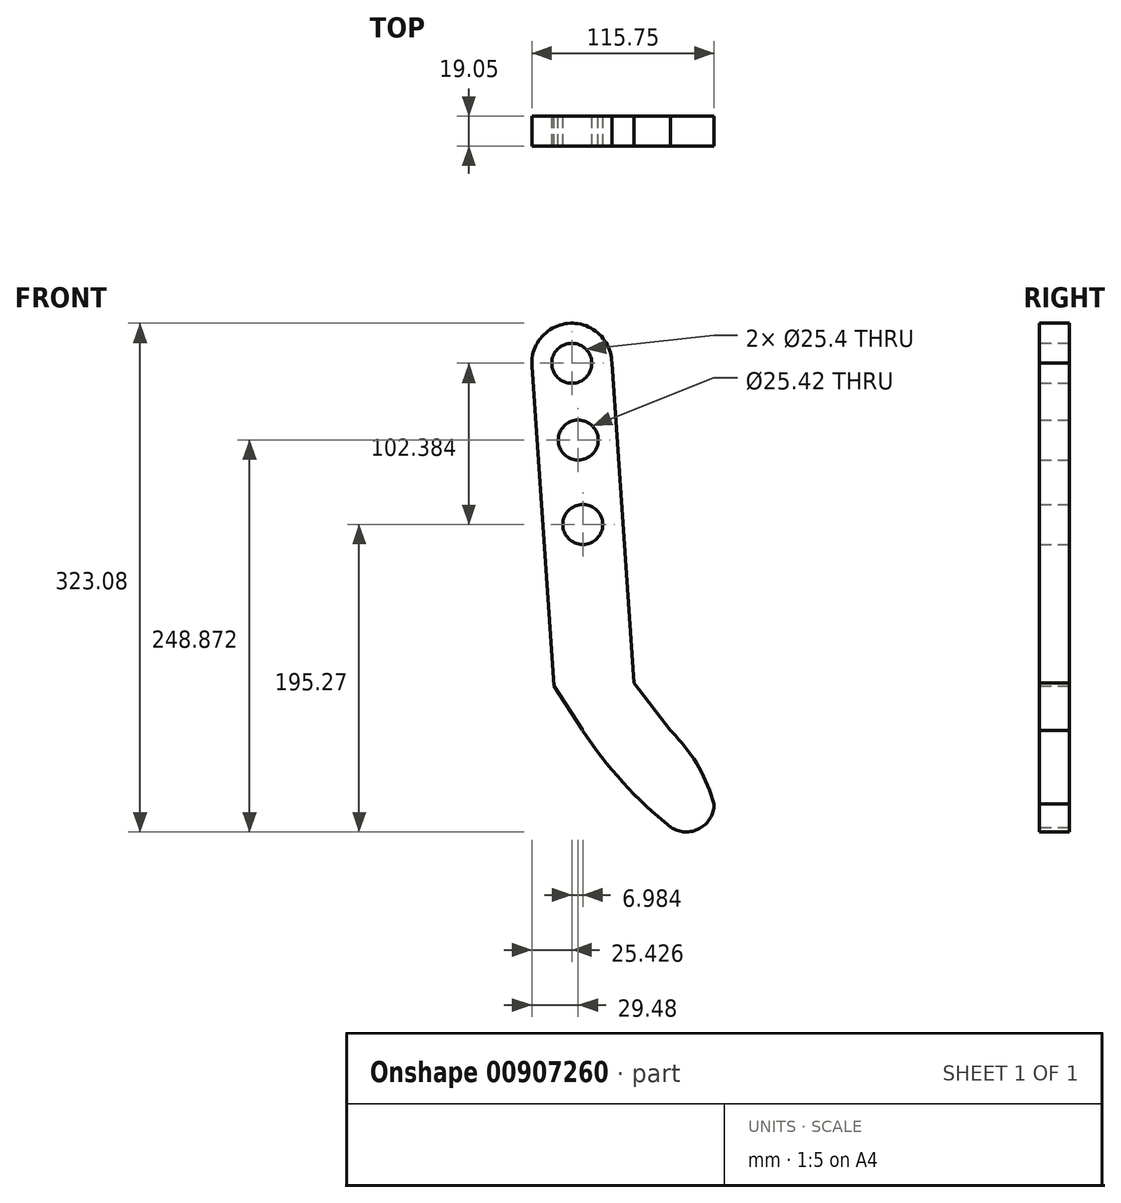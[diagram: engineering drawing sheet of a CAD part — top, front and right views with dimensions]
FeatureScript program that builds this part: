
annotation { "Feature Type Name" : "Feature", "Feature Type Description" : "" }
export const myFeature = defineFeature(function(context is Context, id is Id, definition is map)
    precondition{}
    {
        {
            var Q0;
            Q0=qCreatedBy(makeId("Front.planeOp"),FACE);
            var sketch = newSketch(context, id + "F0", { "sketchPlane" : qUnion([Q0])});
            skLineSegment(sketch, "E0.left", {"start": v(31.28, -85.06) * mm, "end": v(18.44, 102.55) * mm});
            skLineSegment(sketch, "E0.right", {"start": v(-18.44, -102.55) * mm, "end": v(-32.35, 100.65) * mm});
            skPoint(sketch, "E0.middle", {"position": v(0, 0) * mm});
            skArc(sketch, "E1", {"start": v(-32.35, 100.65) * mm, "mid": v(-7.94, 127.79) * mm, "end": v(18.44, 102.55) * mm});
            skPoint(sketch, "E2.middle", {"position": v(32.35, -100.65) * mm});
            skPoint(sketch, "E3.orphan", {"position": v(-9.8, -75.29) * mm});
            skPoint(sketch, "E2.bottom.end.orphan", {"position": v(-9.5, -126.48) * mm});
            skPoint(sketch, "E4.end.orphan", {"position": v(74.49, -126) * mm});
            skLineSegment(sketch, "E5", {"start": v(31.28, -85.06) * mm, "end": v(32.35, -100.65) * mm});
            skPoint(sketch, "E2.top.start.orphan", {"position": v(74.2, -74.82) * mm});
            skLineSegment(sketch, "E6", {"start": v(-18.44, -102.55) * mm, "end": v(27.41, -173.16) * mm});
            skLineSegment(sketch, "E7", {"start": v(27.41, -173.16) * mm, "end": v(83.34, -210.69) * mm});
            skLineSegment(sketch, "E8", {"start": v(83.34, -210.69) * mm, "end": v(83.34, -159.89) * mm});
            skLineSegment(sketch, "E9", {"start": v(83.34, -159.89) * mm, "end": v(55.72, -130.97) * mm});
            skLineSegment(sketch, "E10", {"start": v(55.72, -130.97) * mm, "end": v(32.35, -100.65) * mm});
            skCircle(sketch, "E11", {"center": v(-6.98, 102.38) * mm, "radius": 12.7 * mm});
            skSolve(sketch);
        }
        {
            var Q0;
            Q0 = qSketchRegion(id + "F0", true);
            extrude(context, id + "F1", {"entities" : qUnion([Q0]), "depth" : 19.05 * mm, "offsetDistance" : 25.4 * mm});
        }
        {
            var Q0;
            Q0=makeQuery(id+"F1.opExtrude","SWEPT_EDGE",EDGE,{"disambiguationData":[OSD([sQuery(id+"F0.wireOp",EDGE,"E7"),sQuery(id+"F0.wireOp",EDGE,"E8")])]});
            fillet(context, id + "F2", {"entities" : qUnion([Q0]), "radius" : 17.6 * mm, "tangentPropagation" : true, "allowEdgeOverflow" : false});
        }
        {
            var Q0;
            Q0=makeQuery(id+"F1.opExtrude","SWEPT_EDGE",EDGE,{"disambiguationData":[OSD([sQuery(id+"F0.wireOp",EDGE,"E6"),sQuery(id+"F0.wireOp",EDGE,"E7")])]});
            fillet(context, id + "F3", {"entities" : qUnion([Q0]), "radius" : 257.24 * mm, "tangentPropagation" : true, "allowEdgeOverflow" : false});
        }
        {
            var Q0;
            Q0=makeQuery(id+"F1.opExtrude","SWEPT_EDGE",EDGE,{"disambiguationData":[OSD([sQuery(id+"F0.wireOp",EDGE,"E8"),sQuery(id+"F0.wireOp",EDGE,"E9")])]});
            fillet(context, id + "F4", {"entities" : qUnion([Q0]), "radius" : 101.76 * mm, "tangentPropagation" : true, "allowEdgeOverflow" : false});
        }
        {
            var Q0;
            Q0=qCreatedBy(makeId("Front.planeOp"),FACE);
            var sketch = newSketch(context, id + "F5", { "sketchPlane" : qUnion([Q0])});
            skCircle(sketch, "E12", {"center": v(0, 0) * mm, "radius": 12.7 * mm});
            skSolve(sketch);
        }
        {
            var Q0;
            Q0 = qSketchRegion(id + "F5", true);
            extrude(context, id + "F6", {"entities" : qUnion([Q0]), "operationType" : NewBodyOperationType.REMOVE, "oppositeDirection" : true, "depth" : -50.8 * mm, "offsetDistance" : 25.4 * mm});
        }
        {
            var Q0;
            Q0=qCreatedBy(makeId("Front.planeOp"),FACE);
            var sketch = newSketch(context, id + "F7", { "sketchPlane" : qUnion([Q0])});
            skCircle(sketch, "E13", {"center": v(-2.93, 53.6) * mm, "radius": 12.7 * mm});
            skPoint(sketch, "E13.first.point", {"position": v(-2.7, 66.3) * mm});
            skPoint(sketch, "E13.second.point", {"position": v(-3.1, 40.9) * mm});
            skPoint(sketch, "E13.third.point", {"position": v(-15.63, 53.2) * mm});
            skSolve(sketch);
        }
        {
            var Q0;
            Q0 = qSketchRegion(id + "F7", true);
            extrude(context, id + "F8", {"entities" : qUnion([Q0]), "operationType" : NewBodyOperationType.REMOVE, "depth" : 25.4 * mm, "offsetDistance" : 25.4 * mm});
        }
    });
